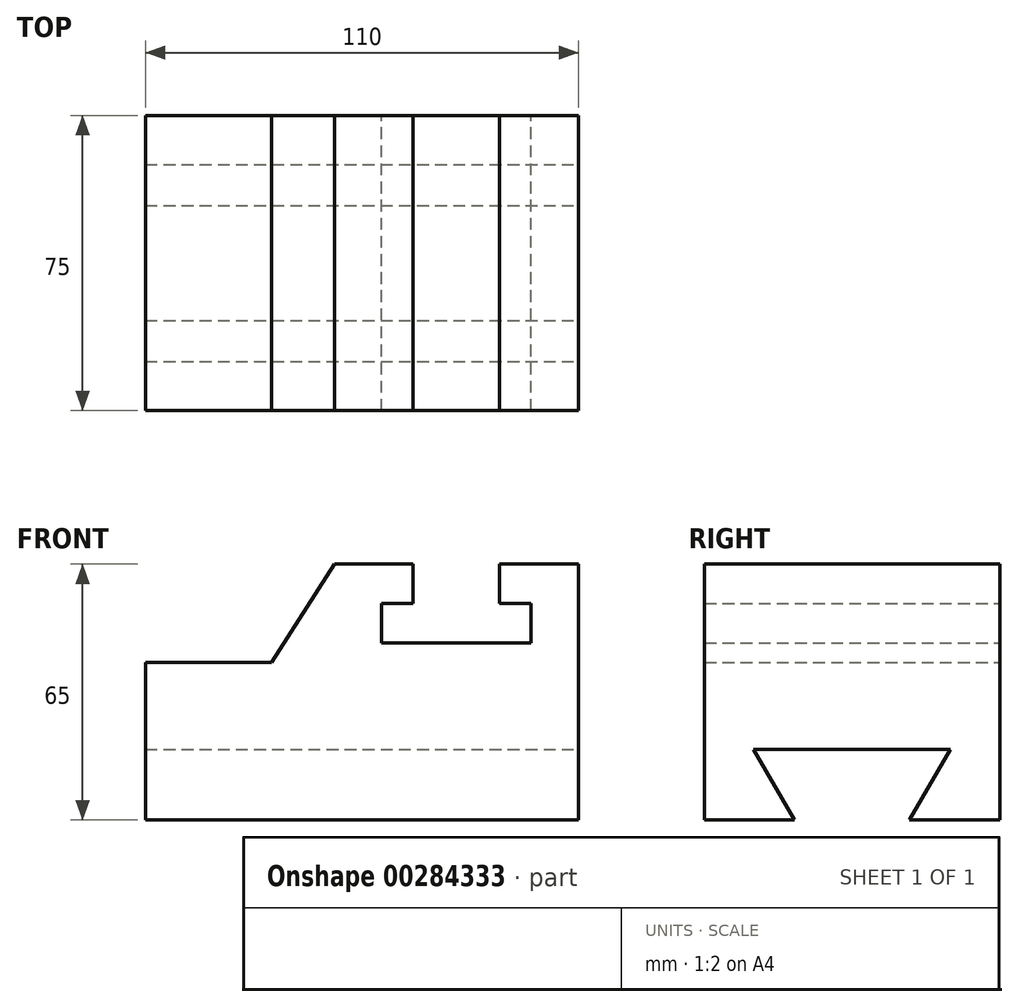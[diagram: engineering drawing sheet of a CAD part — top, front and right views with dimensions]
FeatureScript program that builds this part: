
annotation { "Feature Type Name" : "Feature", "Feature Type Description" : "" }
export const myFeature = defineFeature(function(context is Context, id is Id, definition is map)
    precondition{}
    {
        {
            var Q0;
            Q0=qCreatedBy(makeId("Front.planeOp"),FACE);
            var sketch = newSketch(context, id + "F0", { "sketchPlane" : qUnion([Q0])});
            skLineSegment(sketch, "E0", {"start": v(-54.76, -28.82) * mm, "end": v(-54.76, 11.18) * mm});
            skLineSegment(sketch, "E1", {"start": v(-54.76, 11.18) * mm, "end": v(-22.76, 11.18) * mm});
            skLineSegment(sketch, "E2", {"start": v(-54.76, -28.82) * mm, "end": v(55.24, -28.82) * mm});
            skLineSegment(sketch, "E3", {"start": v(55.24, -28.82) * mm, "end": v(55.24, 36.18) * mm});
            skLineSegment(sketch, "E4", {"start": v(55.24, 36.18) * mm, "end": v(35.24, 36.18) * mm});
            skLineSegment(sketch, "E5", {"start": v(35.24, 36.18) * mm, "end": v(35.24, 26.18) * mm});
            skLineSegment(sketch, "E6", {"start": v(35.24, 26.18) * mm, "end": v(43.24, 26.18) * mm});
            skLineSegment(sketch, "E7", {"start": v(43.24, 26.18) * mm, "end": v(43.24, 16.18) * mm});
            skLineSegment(sketch, "E8", {"start": v(43.24, 16.18) * mm, "end": v(5.24, 16.18) * mm});
            skLineSegment(sketch, "E9", {"start": v(5.24, 16.18) * mm, "end": v(5.24, 26.18) * mm});
            skLineSegment(sketch, "E10", {"start": v(5.24, 26.18) * mm, "end": v(13.24, 26.18) * mm});
            skLineSegment(sketch, "E11", {"start": v(13.24, 26.18) * mm, "end": v(13.24, 36.18) * mm});
            skLineSegment(sketch, "E12", {"start": v(13.24, 36.18) * mm, "end": v(-6.76, 36.18) * mm});
            skLineSegment(sketch, "E13", {"start": v(-6.76, 36.18) * mm, "end": v(-22.76, 11.18) * mm});
            skSolve(sketch);
        }
        {
            var Q0;
            Q0 = qSketchRegion(id + "F0", true);
            extrude(context, id + "F1", {"entities" : qUnion([Q0]), "depth" : 75 * mm});
        }
        {
            var Q0;
            Q0=makeQuery(id+"F1.opExtrude","SWEPT_FACE",FACE,{"disambiguationData":[OSD([sQuery(id+"F0.wireOp",EDGE,"E3")])]});
            var sketch = newSketch(context, id + "F2", { "sketchPlane" : qUnion([Q0])});
            skLineSegment(sketch, "E14", {"start": v(-62.5, -10.82) * mm, "end": v(-12.5, -10.82) * mm});
            skLineSegment(sketch, "E15", {"start": v(-22.9, -28.82) * mm, "end": v(-14.36, -28.82) * mm});
            skLineSegment(sketch, "E16", {"start": v(-22.9, -28.82) * mm, "end": v(-12.5, -10.82) * mm});
            skPoint(sketch, "E17.orphan", {"position": v(-31.42, -28.82) * mm});
            skLineSegment(sketch, "E18", {"start": v(-52.1, -28.82) * mm, "end": v(-62.5, -10.82) * mm});
            skLineSegment(sketch, "E19", {"start": v(-52.1, -28.82) * mm, "end": v(-22.9, -28.82) * mm});
            skSolve(sketch);
        }
        {
            var Q0;
            Q0 = qSketchRegion(id + "F2", true);
            extrude(context, id + "F3", {"entities" : qUnion([Q0]), "operationType" : NewBodyOperationType.REMOVE, "endBound" : BoundingType.THROUGH_ALL, "oppositeDirection" : true, "depth" : 25 * mm});
        }
    });
